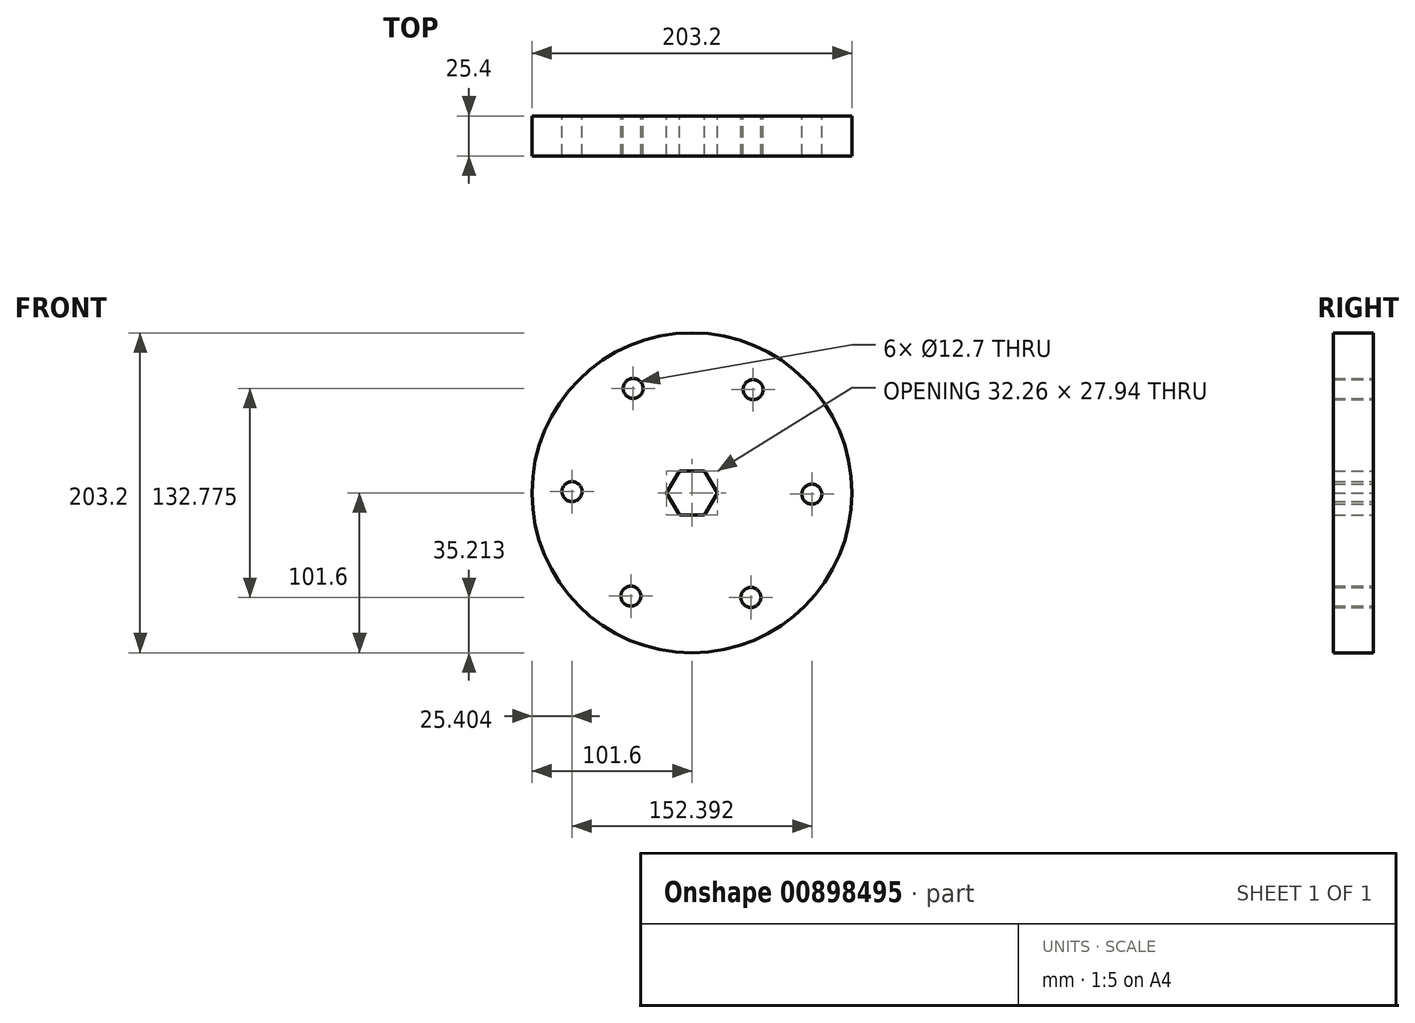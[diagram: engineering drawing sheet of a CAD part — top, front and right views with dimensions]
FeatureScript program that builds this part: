
annotation { "Feature Type Name" : "Feature", "Feature Type Description" : "" }
export const myFeature = defineFeature(function(context is Context, id is Id, definition is map)
    precondition{}
    {
        {
            var Q0;
            Q0=qCreatedBy(makeId("Front.planeOp"),FACE);
            var sketch = newSketch(context, id + "F0", { "sketchPlane" : qUnion([Q0])});
            skCircle(sketch, "E0", {"center": v(0, 0) * mm, "radius": 101.6 * mm});
            skCircle(sketch, "E1", {"center": v(-37.4, 66.39) * mm, "radius": 6.35 * mm});
            skCircle(sketch, "E2", {"center": v(38.8, 65.59) * mm, "radius": 6.35 * mm});
            skCircle(sketch, "E3", {"center": v(76.2, -0.8) * mm, "radius": 6.35 * mm});
            skCircle(sketch, "E4", {"center": v(37.4, -66.39) * mm, "radius": 6.35 * mm});
            skCircle(sketch, "E5", {"center": v(-38.8, -65.59) * mm, "radius": 6.35 * mm});
            skCircle(sketch, "E6", {"center": v(-76.2, 0.8) * mm, "radius": 6.35 * mm});
            skCircle(sketch, "E7.cCircle", {"center": v(0, 0) * mm, "radius": 13.97 * mm, "construction": true});
            skLineSegment(sketch, "E7.0", {"start": v(8.07, -13.97) * mm, "end": v(-8.07, -13.97) * mm});
            skLineSegment(sketch, "E7.1", {"start": v(-8.07, -13.97) * mm, "end": v(-16.13, 0) * mm});
            skLineSegment(sketch, "E7.2", {"start": v(-16.13, 0) * mm, "end": v(-8.07, 13.97) * mm});
            skLineSegment(sketch, "E7.3", {"start": v(-8.07, 13.97) * mm, "end": v(8.07, 13.97) * mm});
            skLineSegment(sketch, "E7.4", {"start": v(8.07, 13.97) * mm, "end": v(16.13, 0) * mm});
            skLineSegment(sketch, "E7.5", {"start": v(16.13, 0) * mm, "end": v(8.07, -13.97) * mm});
            skPoint(sketch, "E7.0.midPoint", {"position": v(0, -13.97) * mm});
            skSolve(sketch);
        }
        {
            var Q0;
            Q0=makeQuery(id+"F0.imprint","IMPRINT",FACE,{"disambiguationData":[TD([[makeQuery(id+"F0.imprint","IMPRINT",EDGE,{"derivedFrom":sQuery(id+"F0.wireOp",EDGE,"E0")}),1.0]])]});
            extrude(context, id + "F1", {"entities" : qUnion([Q0]), "depth" : 25.4 * mm, "offsetDistance" : 25.4 * mm});
        }
    });
